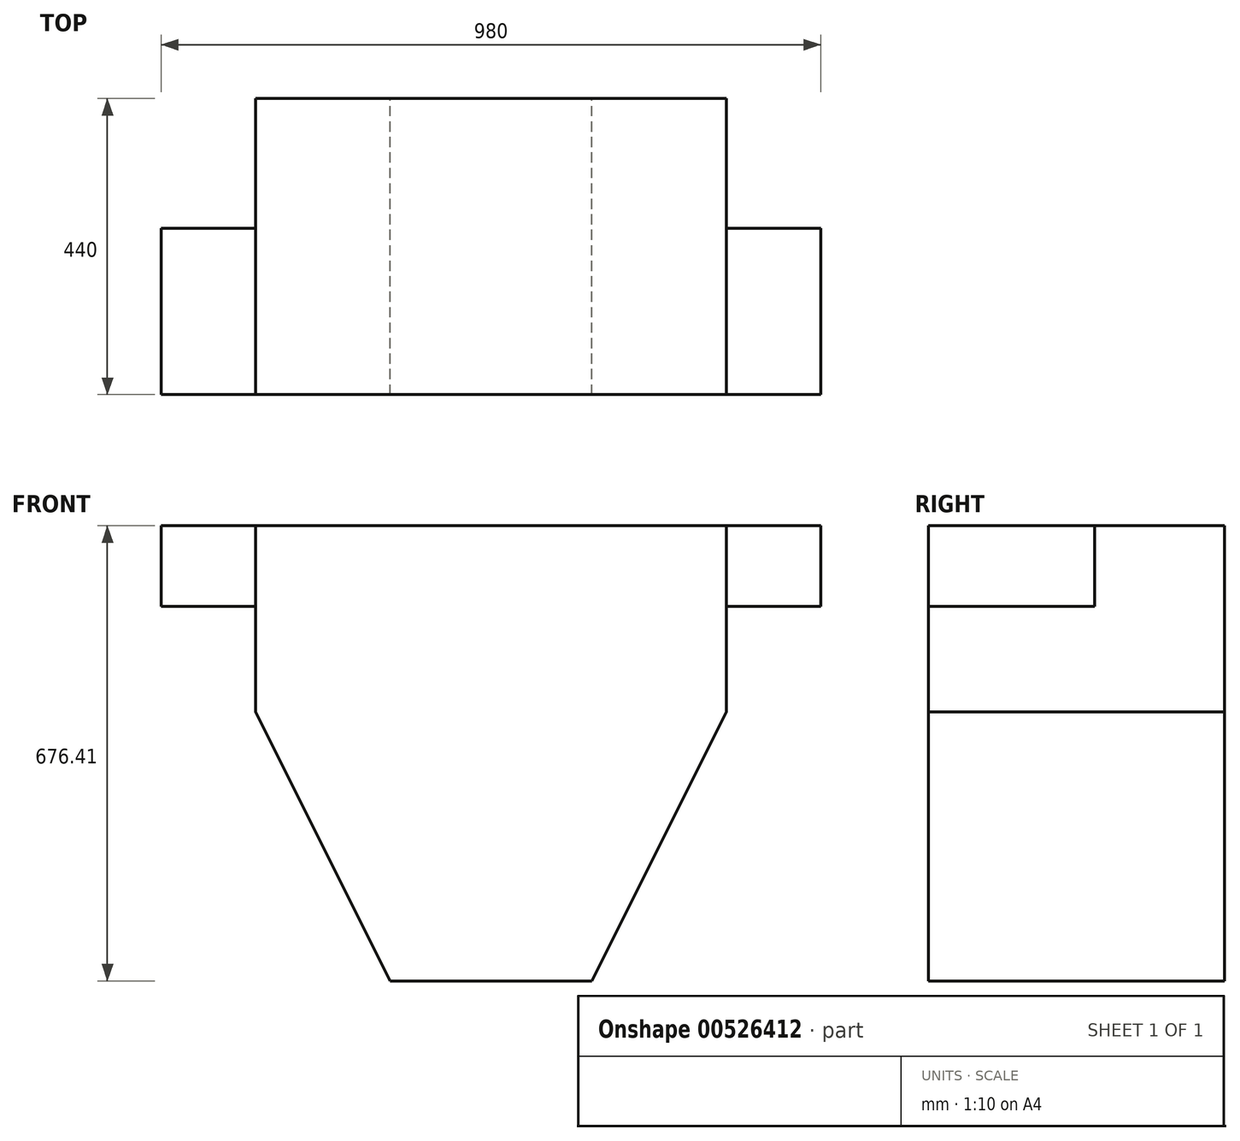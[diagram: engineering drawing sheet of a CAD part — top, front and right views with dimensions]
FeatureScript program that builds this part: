
annotation { "Feature Type Name" : "Feature", "Feature Type Description" : "" }
export const myFeature = defineFeature(function(context is Context, id is Id, definition is map)
    precondition{}
    {
        {
            var Q0;
            Q0=qCreatedBy(makeId("Front.planeOp"),FACE);
            var sketch = newSketch(context, id + "F0", { "sketchPlane" : qUnion([Q0])});
            skLineSegment(sketch, "E0.bottom", {"start": v(139.64, -315.07) * mm, "end": v(-160.36, -315.07) * mm});
            skLineSegment(sketch, "E0.top", {"start": v(339.64, 361.34) * mm, "end": v(-360.36, 361.34) * mm});
            skLineSegment(sketch, "E0.left", {"start": v(339.64, 84.93) * mm, "end": v(339.64, 361.34) * mm});
            skLineSegment(sketch, "E0.right", {"start": v(-360.36, 84.93) * mm, "end": v(-360.36, 361.34) * mm});
            skPoint(sketch, "E0.middle", {"position": v(-10.36, 23.14) * mm});
            skLineSegment(sketch, "E1", {"start": v(-160.36, -315.07) * mm, "end": v(-360.36, 84.93) * mm});
            skLineSegment(sketch, "E2", {"start": v(139.64, -315.07) * mm, "end": v(339.64, 84.93) * mm});
            skPoint(sketch, "E3.orphan", {"position": v(339.64, -315.07) * mm});
            skPoint(sketch, "E4.orphan", {"position": v(-360.36, -315.07) * mm});
            skSolve(sketch);
        }
        {
            var Q0;
            Q0 = qSketchRegion(id + "F0", true);
            extrude(context, id + "F1", {"entities" : qUnion([Q0]), "depth" : 440 * mm, "offsetDistance" : 25.4 * mm});
        }
        {
            var Q0;
            Q0=makeQuery(id+"F1.opExtrude","CAP_FACE",FACE,{"disambiguationData":[OSD([sQuery(id+"F0.wireOp",EDGE,"E0.bottom"),sQuery(id+"F0.wireOp",EDGE,"E0.top"),sQuery(id+"F0.wireOp",EDGE,"E0.left"),sQuery(id+"F0.wireOp",EDGE,"E0.right"),sQuery(id+"F0.wireOp",EDGE,"E1"),sQuery(id+"F0.wireOp",EDGE,"E2")])],"isStart":false});
            var sketch = newSketch(context, id + "F2", { "sketchPlane" : qUnion([Q0])});
            skLineSegment(sketch, "E5", {"start": v(-360.36, 361.34) * mm, "end": v(-500.36, 361.34) * mm});
            skLineSegment(sketch, "E6", {"start": v(-500.36, 361.34) * mm, "end": v(-500.36, 241.34) * mm});
            skLineSegment(sketch, "E7", {"start": v(-500.36, 241.34) * mm, "end": v(-360.36, 241.34) * mm});
            skLineSegment(sketch, "E8", {"start": v(339.64, 361.34) * mm, "end": v(479.64, 361.34) * mm});
            skLineSegment(sketch, "E9", {"start": v(479.64, 361.34) * mm, "end": v(479.64, 241.34) * mm});
            skLineSegment(sketch, "E10", {"start": v(479.64, 241.34) * mm, "end": v(339.64, 241.34) * mm});
            skSolve(sketch);
        }
        {
            var Q0;
            Q0 = qSketchRegion(id + "F2", true);
            var Q1;
            {var subQ0=sQuery(id+"F2.wireOp",EDGE,"E5");Q1=makeQuery(id+"F2.imprint","IMPRINT",FACE,{"disambiguationData":[TD([[makeQuery(id+"F2.imprint","IMPRINT",EDGE,{"derivedFrom":subQ0}),1.0]])]});}
            var Q2;
            {var subQ0=sQuery(id+"F2.wireOp",EDGE,"E8");Q2=makeQuery(id+"F2.imprint","IMPRINT",FACE,{"disambiguationData":[TD([[makeQuery(id+"F2.imprint","IMPRINT",EDGE,{"derivedFrom":subQ0}),-1.0]])]});}
            extrude(context, id + "F3", {"entities" : qUnion([Q0, Q1, Q2]), "oppositeDirection" : true, "depth" : 247.47 * mm, "offsetDistance" : 25.4 * mm});
        }
    });
